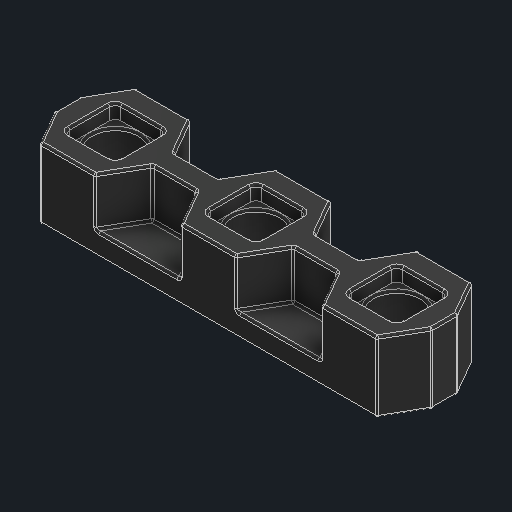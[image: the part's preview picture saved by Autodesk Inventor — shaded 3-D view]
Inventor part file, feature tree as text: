
AUTODESK INVENTOR PART (.ipt)
format: ipt  version: 2025 (Build 290162000, 162)  size: 499,712 bytes
history: native  units: in
note: dims shown in document units (in); Inventor stores cm internally (conversion verified against a paired STEP export)
features: other x3, sketch x1
ambient origin geometry x8: Origin, YZ Plane, XZ Plane, XY Plane, X Axis, Y Axis, Z Axis, Center Point
bodies: Solid1 (feature_tree)
feature tree (4):
  other  "Bearing Flat Low Profile.ipt"
  other  "Solid1::Bearing Flat Low Profile.ipt"
  other  "TaggingFeature1"
  sketch  "Sketch1"  dims[d0=0.3937in]
